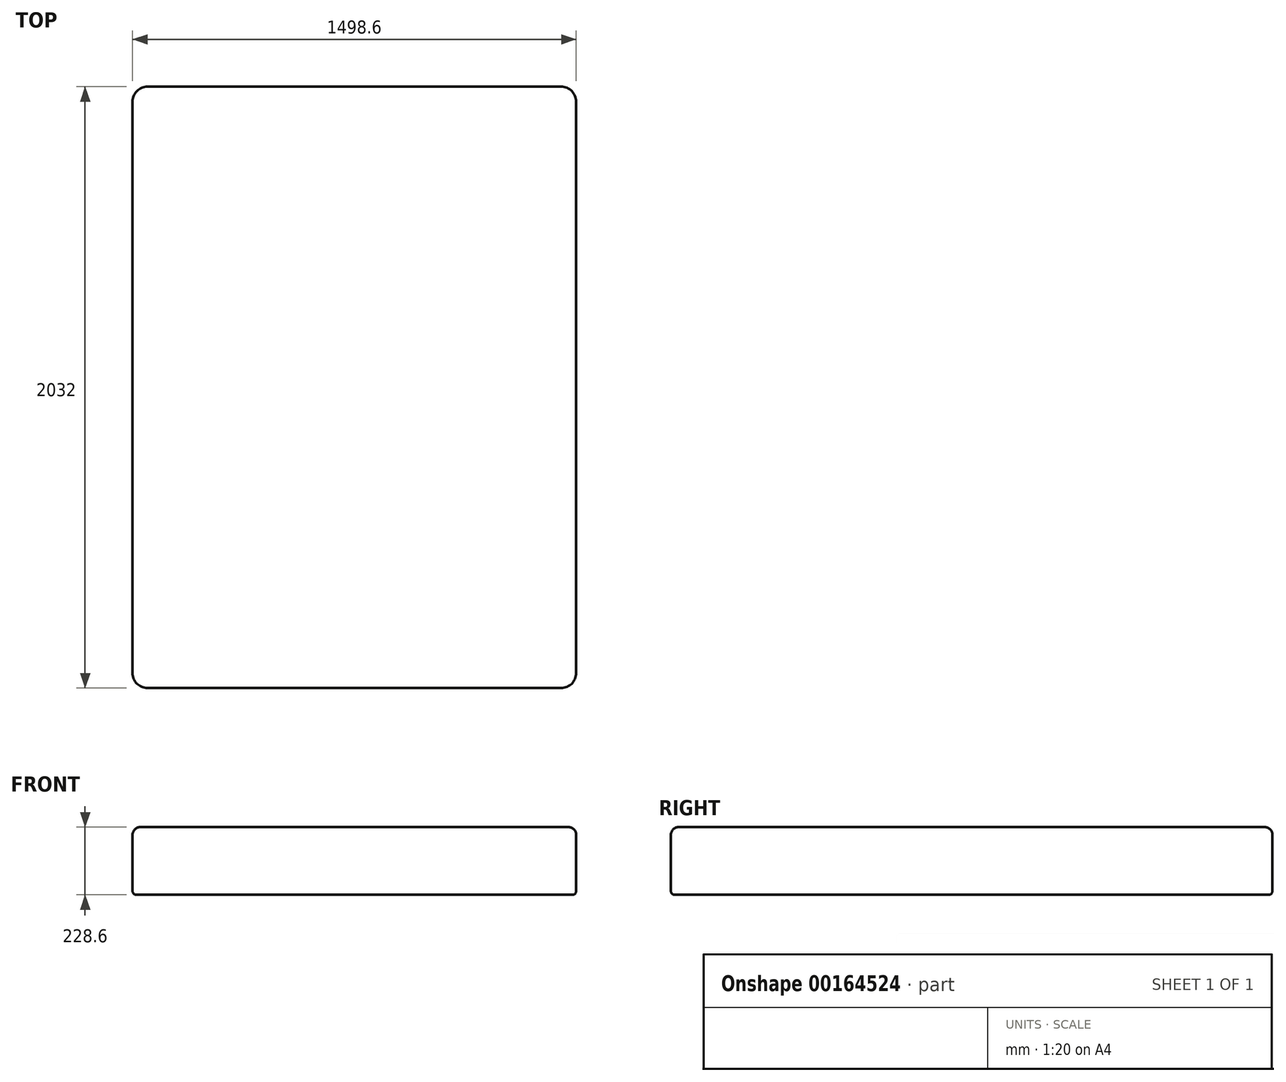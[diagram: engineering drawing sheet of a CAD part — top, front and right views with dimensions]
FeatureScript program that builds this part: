
annotation { "Feature Type Name" : "Feature", "Feature Type Description" : "" }
export const myFeature = defineFeature(function(context is Context, id is Id, definition is map)
    precondition{}
    {
        {
            var Q0;
            Q0=qCreatedBy(makeId("Top.planeOp"),FACE);
            var sketch = newSketch(context, id + "F0", { "sketchPlane" : qUnion([Q0])});
            skLineSegment(sketch, "E0.bottom", {"start": v(749.3, 1016) * mm, "end": v(-749.3, 1016) * mm});
            skLineSegment(sketch, "E0.top", {"start": v(749.3, -1016) * mm, "end": v(-749.3, -1016) * mm});
            skLineSegment(sketch, "E0.left", {"start": v(749.3, 1016) * mm, "end": v(749.3, -1016) * mm});
            skLineSegment(sketch, "E0.right", {"start": v(-749.3, 1016) * mm, "end": v(-749.3, -1016) * mm});
            skPoint(sketch, "E0.middle", {"position": v(0, 0) * mm});
            skSolve(sketch);
        }
        {
            var Q0;
            Q0 = qSketchRegion(id + "F0", true);
            extrude(context, id + "F1", {"entities" : qUnion([Q0]), "depth" : 228.6 * mm});
        }
        {
            var Q0;
            Q0=makeQuery(id+"F1.opExtrude","CAP_EDGE",EDGE,{"disambiguationData":[OSD([sQuery(id+"F0.wireOp",EDGE,"E0.right")])],"isStart":false});
            var Q1;
            Q1=makeQuery(id+"F1.opExtrude","CAP_EDGE",EDGE,{"disambiguationData":[OSD([sQuery(id+"F0.wireOp",EDGE,"E0.top")])],"isStart":false});
            var Q2;
            Q2=makeQuery(id+"F1.opExtrude","CAP_EDGE",EDGE,{"disambiguationData":[OSD([sQuery(id+"F0.wireOp",EDGE,"E0.left")])],"isStart":false});
            var Q3;
            Q3=makeQuery(id+"F1.opExtrude","CAP_EDGE",EDGE,{"disambiguationData":[OSD([sQuery(id+"F0.wireOp",EDGE,"E0.bottom")])],"isStart":false});
            fillet(context, id + "F2", {"entities" : qUnion([Q0, Q1, Q2, Q3]), "radius" : 25.4 * mm, "tangentPropagation" : true, "allowEdgeOverflow" : false});
        }
        {
            var Q0;
            Q0=makeQuery(id+"F1.opExtrude","SWEPT_EDGE",EDGE,{"disambiguationData":[OSD([sQuery(id+"F0.wireOp",EDGE,"E0.top"),sQuery(id+"F0.wireOp",EDGE,"E0.right")])]});
            var Q1;
            Q1=makeQuery(id+"F1.opExtrude","SWEPT_EDGE",EDGE,{"disambiguationData":[OSD([sQuery(id+"F0.wireOp",EDGE,"E0.top"),sQuery(id+"F0.wireOp",EDGE,"E0.left")])]});
            var Q2;
            Q2=makeQuery(id+"F1.opExtrude","SWEPT_EDGE",EDGE,{"disambiguationData":[OSD([sQuery(id+"F0.wireOp",EDGE,"E0.bottom"),sQuery(id+"F0.wireOp",EDGE,"E0.right")])]});
            var Q3;
            Q3=makeQuery(id+"F1.opExtrude","SWEPT_EDGE",EDGE,{"disambiguationData":[OSD([sQuery(id+"F0.wireOp",EDGE,"E0.bottom"),sQuery(id+"F0.wireOp",EDGE,"E0.left")])]});
            fillet(context, id + "F3", {"entities" : qUnion([Q0, Q1, Q2, Q3]), "radius" : 50.8 * mm, "tangentPropagation" : true, "allowEdgeOverflow" : false});
        }
        {
            var Q0;
            Q0=makeQuery(id+"F1.opExtrude","CAP_EDGE",EDGE,{"disambiguationData":[OSD([sQuery(id+"F0.wireOp",EDGE,"E0.bottom")])],"isStart":true});
            var Q1;
            Q1=makeQuery(id+"F1.opExtrude","CAP_EDGE",EDGE,{"disambiguationData":[OSD([sQuery(id+"F0.wireOp",EDGE,"E0.right")])],"isStart":true});
            var Q2;
            Q2=makeQuery(id+"F1.opExtrude","CAP_EDGE",EDGE,{"disambiguationData":[OSD([sQuery(id+"F0.wireOp",EDGE,"E0.top")])],"isStart":true});
            fillet(context, id + "F4", {"entities" : qUnion([Q0, Q1, Q2]), "radius" : 12.7 * mm, "tangentPropagation" : true, "allowEdgeOverflow" : false});
        }
    });
